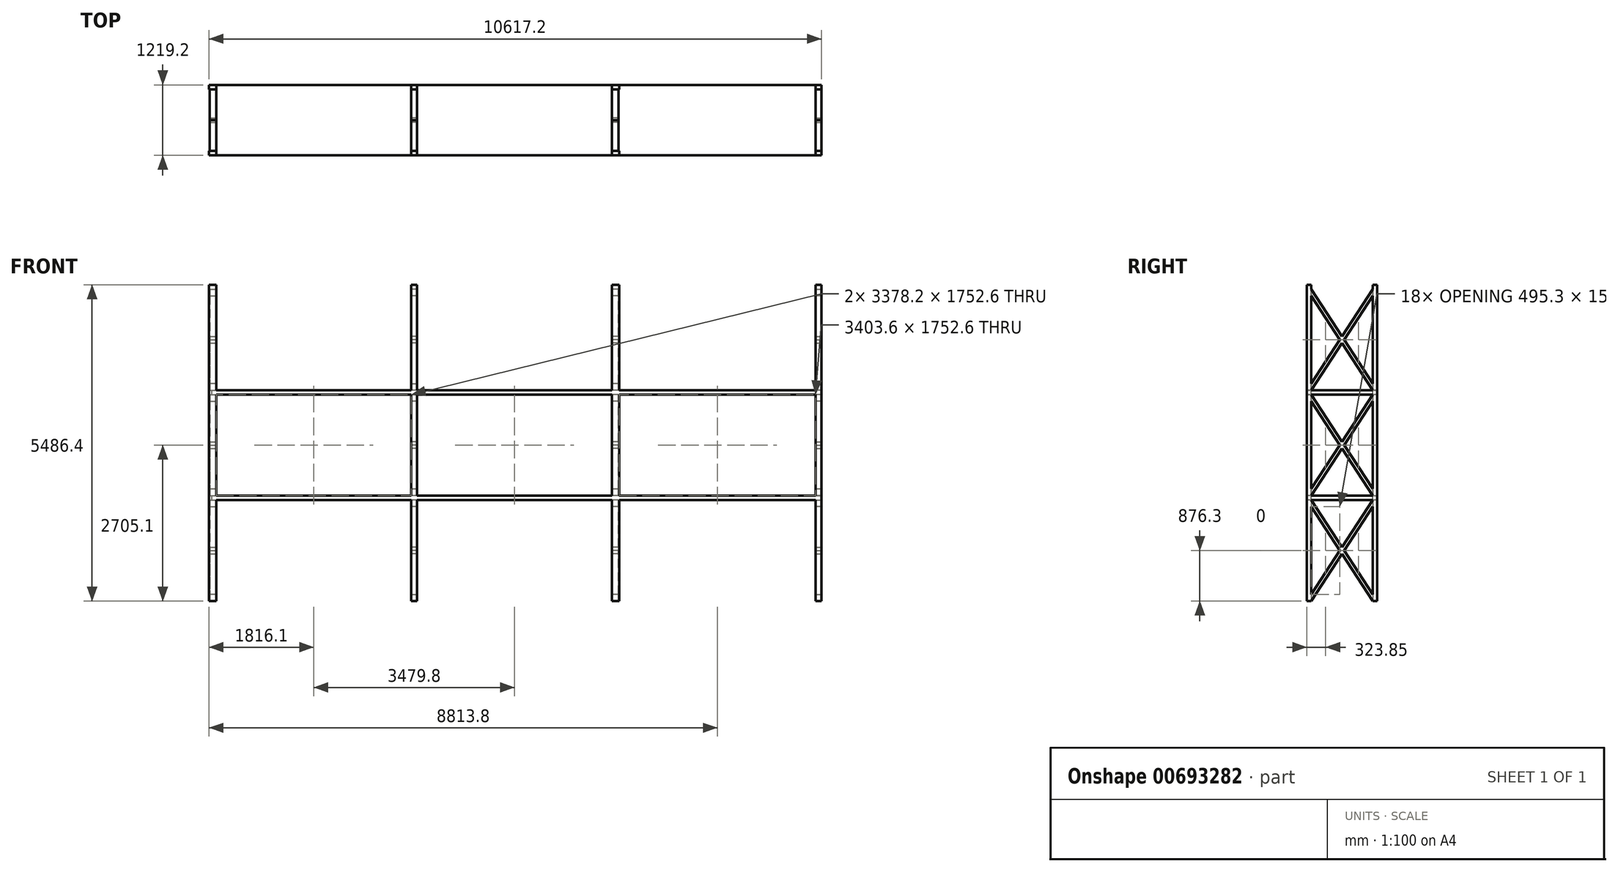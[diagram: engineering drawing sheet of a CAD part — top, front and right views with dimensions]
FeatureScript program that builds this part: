
annotation { "Feature Type Name" : "Feature", "Feature Type Description" : "" }
export const myFeature = defineFeature(function(context is Context, id is Id, definition is map)
    precondition{}
    {
        {
            var Q0;
            Q0=qCreatedBy(makeId("Front.planeOp"),FACE);
            var sketch = newSketch(context, id + "F0", { "sketchPlane" : qUnion([Q0])});
            skLineSegment(sketch, "E0.bottom", {"start": v(0, 0) * mm, "end": v(76.2, 0) * mm, "construction": true});
            skLineSegment(sketch, "E0.top", {"start": v(0, 5486.4) * mm, "end": v(76.2, 5486.4) * mm, "construction": true});
            skLineSegment(sketch, "E0.left", {"start": v(0, 0) * mm, "end": v(0, 5486.4) * mm, "construction": true});
            skLineSegment(sketch, "E0.right", {"start": v(76.2, 0) * mm, "end": v(76.2, 5486.4) * mm, "construction": true});
            skLineSegment(sketch, "E1.left", {"start": v(0, 5486.4) * mm, "end": v(0, 5410.2) * mm});
            skLineSegment(sketch, "E1.right", {"start": v(7010.4, 5486.4) * mm, "end": v(7010.4, 5410.2) * mm, "construction": true});
            skLineSegment(sketch, "E2.bottom", {"start": v(6934.2, 0) * mm, "end": v(7010.4, 0) * mm, "construction": true});
            skLineSegment(sketch, "E2.left", {"start": v(6934.2, 0) * mm, "end": v(6934.2, 5486.4) * mm, "construction": true});
            skLineSegment(sketch, "E2.right", {"start": v(7010.4, 0) * mm, "end": v(7010.4, 5334) * mm, "construction": true});
            skPoint(sketch, "E3", {"position": v(0, 1752.6) * mm});
            skPoint(sketch, "E4", {"position": v(0, 3581.4) * mm});
            skLineSegment(sketch, "E5.bottom", {"start": v(0, 1752.6) * mm, "end": v(7010.4, 1752.6) * mm});
            skLineSegment(sketch, "E5.top", {"start": v(0, 1828.8) * mm, "end": v(7010.4, 1828.8) * mm});
            skLineSegment(sketch, "E5.left", {"start": v(0, 1752.6) * mm, "end": v(0, 1828.8) * mm});
            skLineSegment(sketch, "E5.right", {"start": v(7010.4, 1752.6) * mm, "end": v(7010.4, 1828.8) * mm});
            skLineSegment(sketch, "E6.bottom", {"start": v(0, 3581.4) * mm, "end": v(7010.4, 3581.4) * mm});
            skLineSegment(sketch, "E6.top", {"start": v(0, 3657.6) * mm, "end": v(7010.4, 3657.6) * mm});
            skLineSegment(sketch, "E6.left", {"start": v(0, 3581.4) * mm, "end": v(0, 3657.6) * mm});
            skLineSegment(sketch, "E6.right", {"start": v(7010.4, 3581.4) * mm, "end": v(7010.4, 3657.6) * mm});
            skSolve(sketch);
        }
        {
            var Q0;
            Q0 = qSketchRegion(id + "F0", true);
            extrude(context, id + "F1", {"entities" : qUnion([Q0]), "oppositeDirection" : true, "depth" : 1219.2 * mm, "offsetDistance" : 25.4 * mm});
        }
        {
            var Q0;
            Q0=makeQuery(id+"F1.opExtrude","SWEPT_FACE",FACE,{"disambiguationData":[OSD([sQuery(id+"F0.wireOp",EDGE,"E6.left")])]});
            var sketch = newSketch(context, id + "F2", { "sketchPlane" : qUnion([Q0])});
            skLineSegment(sketch, "E7.bottom", {"start": v(0, 0) * mm, "end": v(-76.2, 0) * mm});
            skLineSegment(sketch, "E7.top", {"start": v(0, 5486.4) * mm, "end": v(-76.2, 5486.4) * mm});
            skLineSegment(sketch, "E7.left", {"start": v(0, 0) * mm, "end": v(0, 5486.4) * mm});
            skLineSegment(sketch, "E7.right", {"start": v(-76.2, 0) * mm, "end": v(-76.2, 5486.4) * mm});
            skLineSegment(sketch, "E8.bottom", {"start": v(-1219.2, 0) * mm, "end": v(-1143, 0) * mm});
            skLineSegment(sketch, "E8.top", {"start": v(-1219.2, 5486.4) * mm, "end": v(-1143, 5486.4) * mm});
            skLineSegment(sketch, "E8.left", {"start": v(-1219.2, 0) * mm, "end": v(-1219.2, 5486.4) * mm});
            skLineSegment(sketch, "E8.right", {"start": v(-1143, 0) * mm, "end": v(-1143, 5486.4) * mm});
            skSolve(sketch);
        }
        {
            var Q0;
            Q0 = qSketchRegion(id + "F2", true);
            extrude(context, id + "F3", {"entities" : qUnion([Q0]), "oppositeDirection" : true, "depth" : 76.2 * mm, "offsetDistance" : 25.4 * mm, "hasSecondDirection" : true, "secondDirectionOppositeDirection" : false, "secondDirectionDepth" : 50.8 * mm});
        }
        {
            var Q0;
            Q0=makeQuery(id+"F1.opExtrude","SWEPT_FACE",FACE,{"disambiguationData":[OSD([sQuery(id+"F0.wireOp",EDGE,"E6.right")])]});
            var sketch = newSketch(context, id + "F4", { "sketchPlane" : qUnion([Q0])});
            skLineSegment(sketch, "E9.bottom", {"start": v(0, 0) * mm, "end": v(76.2, 0) * mm});
            skLineSegment(sketch, "E9.top", {"start": v(0, 5486.4) * mm, "end": v(76.2, 5486.4) * mm});
            skLineSegment(sketch, "E9.left", {"start": v(0, 0) * mm, "end": v(0, 5486.4) * mm});
            skLineSegment(sketch, "E9.right", {"start": v(76.2, 0) * mm, "end": v(76.2, 5486.4) * mm});
            skLineSegment(sketch, "E10.bottom", {"start": v(1219.2, 0) * mm, "end": v(1143, 0) * mm});
            skLineSegment(sketch, "E10.top", {"start": v(1219.2, 5486.4) * mm, "end": v(1143, 5486.4) * mm});
            skLineSegment(sketch, "E10.left", {"start": v(1219.2, 0) * mm, "end": v(1219.2, 5486.4) * mm});
            skLineSegment(sketch, "E10.right", {"start": v(1143, 0) * mm, "end": v(1143, 5486.4) * mm});
            skSolve(sketch);
        }
        {
            var Q0;
            Q0 = qSketchRegion(id + "F4", true);
            extrude(context, id + "F5", {"entities" : qUnion([Q0]), "depth" : 50.8 * mm, "offsetDistance" : 25.4 * mm, "hasSecondDirection" : true, "secondDirectionOppositeDirection" : true, "secondDirectionDepth" : 76.2 * mm});
        }
        {
            var Q0;
            Q0=makeQuery(id+"F1.opExtrude","SWEPT_FACE",FACE,{"disambiguationData":[OSD([sQuery(id+"F0.wireOp",EDGE,"E5.left")])]});
            var sketch = newSketch(context, id + "F6", { "sketchPlane" : qUnion([Q0])});
            skPoint(sketch, "E11", {"position": v(-76.2, 0) * mm});
            skPoint(sketch, "E12", {"position": v(-1219.2, 1752.6) * mm});
            skPoint(sketch, "E13", {"position": v(-1219.2, 1828.8) * mm});
            skPoint(sketch, "E14", {"position": v(0, 1752.6) * mm});
            skPoint(sketch, "E15", {"position": v(-1219.2, 0) * mm});
            skPoint(sketch, "E16", {"position": v(-1143, 0) * mm});
            skLineSegment(sketch, "E17", {"start": v(-1219.2, 1752.6) * mm, "end": v(-76.2, 0) * mm});
            skLineSegment(sketch, "E18", {"start": v(0, 1752.6) * mm, "end": v(-1143, 0) * mm});
            skPoint(sketch, "E19", {"position": v(-76.2, 1828.8) * mm});
            skPoint(sketch, "E20", {"position": v(-1143, 1828.8) * mm});
            skPoint(sketch, "E21", {"position": v(-76.2, 1752.6) * mm});
            skPoint(sketch, "E22", {"position": v(-1143, 1752.6) * mm});
            skLineSegment(sketch, "E23", {"start": v(-1219.2, 1752.6) * mm, "end": v(-1143, 1752.6) * mm});
            skLineSegment(sketch, "E24", {"start": v(0, 1752.6) * mm, "end": v(-76.2, 1752.6) * mm});
            skLineSegment(sketch, "E25", {"start": v(-1143, 0) * mm, "end": v(-1219.2, 0) * mm});
            skLineSegment(sketch, "E26", {"start": v(-1219.2, 0) * mm, "end": v(-76.2, 1752.6) * mm});
            skLineSegment(sketch, "E27", {"start": v(-1143, 1752.6) * mm, "end": v(0, 0) * mm});
            skLineSegment(sketch, "E28", {"start": v(-76.2, 0) * mm, "end": v(0, 0) * mm});
            skSolve(sketch);
        }
        {
            var Q0;
            Q0 = qSketchRegion(id + "F6", true);
            extrude(context, id + "F7", {"entities" : qUnion([Q0]), "depth" : 38.1 * mm, "offsetDistance" : 25.4 * mm, "hasSecondDirection" : true, "secondDirectionOppositeDirection" : true, "secondDirectionDepth" : 76.2 * mm});
        }
        {
            var Q0;
            Q0=makeQuery(id+"F1.opExtrude","SWEPT_FACE",FACE,{"disambiguationData":[OSD([sQuery(id+"F0.wireOp",EDGE,"E5.left")])]});
            var sketch = newSketch(context, id + "F8", { "sketchPlane" : qUnion([Q0])});
            skPoint(sketch, "E29", {"position": v(-1219.2, 3581.4) * mm});
            skLineSegment(sketch, "E30", {"start": v(-1219.2, 3581.4) * mm, "end": v(-76.2, 1828.8) * mm});
            skLineSegment(sketch, "E31", {"start": v(0, 3581.4) * mm, "end": v(-1143, 1828.8) * mm});
            skPoint(sketch, "E32", {"position": v(-1143, 3581.4) * mm});
            skLineSegment(sketch, "E33", {"start": v(-1219.2, 1828.8) * mm, "end": v(-76.2, 3581.4) * mm});
            skLineSegment(sketch, "E34", {"start": v(-1143, 3581.4) * mm, "end": v(0, 1828.8) * mm});
            skLineSegment(sketch, "E35", {"start": v(-1219.2, 3581.4) * mm, "end": v(-1143, 3581.4) * mm});
            skLineSegment(sketch, "E36", {"start": v(-76.2, 3581.4) * mm, "end": v(0, 3581.4) * mm});
            skLineSegment(sketch, "E37", {"start": v(-76.2, 1828.8) * mm, "end": v(0, 1828.8) * mm});
            skLineSegment(sketch, "E38", {"start": v(-1143, 1828.8) * mm, "end": v(-1219.2, 1828.8) * mm});
            skSolve(sketch);
        }
        {
            var Q0;
            Q0 = qSketchRegion(id + "F8", true);
            extrude(context, id + "F9", {"entities" : qUnion([Q0]), "depth" : 38.1 * mm, "offsetDistance" : 25.4 * mm, "hasSecondDirection" : true, "secondDirectionOppositeDirection" : true, "secondDirectionDepth" : 76.2 * mm});
        }
        {
            var Q0;
            Q0=makeQuery(id+"F1.opExtrude","SWEPT_FACE",FACE,{"disambiguationData":[OSD([sQuery(id+"F0.wireOp",EDGE,"E6.left")])]});
            var sketch = newSketch(context, id + "F10", { "sketchPlane" : qUnion([Q0])});
            skPoint(sketch, "E39", {"position": v(-1219.2, 5410.2) * mm});
            skLineSegment(sketch, "E40", {"start": v(-1219.2, 5410.2) * mm, "end": v(-76.2, 3657.6) * mm});
            skLineSegment(sketch, "E41", {"start": v(0, 5410.2) * mm, "end": v(-1143, 3657.6) * mm});
            skPoint(sketch, "E42", {"position": v(-1143, 5410.2) * mm});
            skLineSegment(sketch, "E43", {"start": v(-1219.2, 3657.6) * mm, "end": v(-76.2, 5410.2) * mm});
            skLineSegment(sketch, "E44", {"start": v(-1143, 5410.2) * mm, "end": v(0, 3657.6) * mm});
            skLineSegment(sketch, "E45", {"start": v(-1219.2, 5410.2) * mm, "end": v(-1143, 5410.2) * mm});
            skLineSegment(sketch, "E46", {"start": v(-76.2, 5410.2) * mm, "end": v(0, 5410.2) * mm});
            skLineSegment(sketch, "E47", {"start": v(-76.2, 3657.6) * mm, "end": v(0, 3657.6) * mm});
            skLineSegment(sketch, "E48", {"start": v(-1143, 3657.6) * mm, "end": v(-1219.2, 3657.6) * mm});
            skSolve(sketch);
        }
        {
            var Q0;
            Q0 = qSketchRegion(id + "F10", true);
            extrude(context, id + "F11", {"entities" : qUnion([Q0]), "depth" : 38.1 * mm, "offsetDistance" : 25.4 * mm, "hasSecondDirection" : true, "secondDirectionOppositeDirection" : true, "secondDirectionDepth" : 76.2 * mm});
        }
        {
            var Q0;
            Q0=makeQuery(id+"F1.opExtrude","SWEPT_FACE",FACE,{"disambiguationData":[OSD([sQuery(id+"F0.wireOp",EDGE,"E5.right")])]});
            var sketch = newSketch(context, id + "F12", { "sketchPlane" : qUnion([Q0])});
            skPoint(sketch, "E49", {"position": v(0, 1752.6) * mm});
            skLineSegment(sketch, "E50", {"start": v(0, 1752.6) * mm, "end": v(1143, 0) * mm});
            skLineSegment(sketch, "E51", {"start": v(1219.2, 1752.6) * mm, "end": v(76.2, 0) * mm});
            skPoint(sketch, "E52", {"position": v(76.2, 1752.6) * mm});
            skLineSegment(sketch, "E53", {"start": v(0, 0) * mm, "end": v(1143, 1752.6) * mm});
            skLineSegment(sketch, "E54", {"start": v(76.2, 1752.6) * mm, "end": v(1219.2, 0) * mm});
            skLineSegment(sketch, "E55", {"start": v(0, 1752.6) * mm, "end": v(76.2, 1752.6) * mm});
            skLineSegment(sketch, "E56", {"start": v(1143, 1752.6) * mm, "end": v(1219.2, 1752.6) * mm});
            skLineSegment(sketch, "E57", {"start": v(1143, 0) * mm, "end": v(1219.2, 0) * mm});
            skLineSegment(sketch, "E58", {"start": v(76.2, 0) * mm, "end": v(0, 0) * mm});
            skSolve(sketch);
        }
        {
            var Q0;
            Q0 = qSketchRegion(id + "F12", true);
            extrude(context, id + "F13", {"entities" : qUnion([Q0]), "depth" : 38.1 * mm, "offsetDistance" : 25.4 * mm, "hasSecondDirection" : true, "secondDirectionOppositeDirection" : true, "secondDirectionDepth" : 76.2 * mm});
        }
        {
            var Q0;
            Q0=makeQuery(id+"F1.opExtrude","SWEPT_FACE",FACE,{"disambiguationData":[OSD([sQuery(id+"F0.wireOp",EDGE,"E5.right")])]});
            var sketch = newSketch(context, id + "F14", { "sketchPlane" : qUnion([Q0])});
            skPoint(sketch, "E59", {"position": v(0, 3581.4) * mm});
            skLineSegment(sketch, "E60", {"start": v(0, 3581.4) * mm, "end": v(1143, 1828.8) * mm});
            skLineSegment(sketch, "E61", {"start": v(1219.2, 3581.4) * mm, "end": v(76.2, 1828.8) * mm});
            skPoint(sketch, "E62", {"position": v(76.2, 3581.4) * mm});
            skLineSegment(sketch, "E63", {"start": v(0, 1828.8) * mm, "end": v(1143, 3581.4) * mm});
            skLineSegment(sketch, "E64", {"start": v(76.2, 3581.4) * mm, "end": v(1219.2, 1828.8) * mm});
            skLineSegment(sketch, "E65", {"start": v(0, 3581.4) * mm, "end": v(76.2, 3581.4) * mm});
            skLineSegment(sketch, "E66", {"start": v(1143, 3581.4) * mm, "end": v(1219.2, 3581.4) * mm});
            skLineSegment(sketch, "E67", {"start": v(1143, 1828.8) * mm, "end": v(1219.2, 1828.8) * mm});
            skLineSegment(sketch, "E68", {"start": v(76.2, 1828.8) * mm, "end": v(0, 1828.8) * mm});
            skSolve(sketch);
        }
        {
            var Q0;
            Q0 = qSketchRegion(id + "F14", true);
            extrude(context, id + "F15", {"entities" : qUnion([Q0]), "depth" : 38.1 * mm, "offsetDistance" : 25.4 * mm, "hasSecondDirection" : true, "secondDirectionOppositeDirection" : true, "secondDirectionDepth" : 76.2 * mm});
        }
        {
            var Q0;
            Q0=makeQuery(id+"F1.opExtrude","SWEPT_FACE",FACE,{"disambiguationData":[OSD([sQuery(id+"F0.wireOp",EDGE,"E6.right")])]});
            var sketch = newSketch(context, id + "F16", { "sketchPlane" : qUnion([Q0])});
            skPoint(sketch, "E69", {"position": v(0, 5410.2) * mm});
            skLineSegment(sketch, "E70", {"start": v(0, 5410.2) * mm, "end": v(1143, 3657.6) * mm});
            skLineSegment(sketch, "E71", {"start": v(1219.2, 5410.2) * mm, "end": v(76.2, 3657.6) * mm});
            skPoint(sketch, "E72", {"position": v(76.2, 5410.2) * mm});
            skLineSegment(sketch, "E73", {"start": v(0, 3657.6) * mm, "end": v(1143, 5410.2) * mm});
            skLineSegment(sketch, "E74", {"start": v(76.2, 5410.2) * mm, "end": v(1219.2, 3657.6) * mm});
            skLineSegment(sketch, "E75", {"start": v(0, 5410.2) * mm, "end": v(76.2, 5410.2) * mm});
            skLineSegment(sketch, "E76", {"start": v(1143, 5410.2) * mm, "end": v(1219.2, 5410.2) * mm});
            skLineSegment(sketch, "E77", {"start": v(1143, 3657.6) * mm, "end": v(1219.2, 3657.6) * mm});
            skLineSegment(sketch, "E78", {"start": v(76.2, 3657.6) * mm, "end": v(0, 3657.6) * mm});
            skSolve(sketch);
        }
        {
            var Q0;
            Q0 = qSketchRegion(id + "F16", true);
            extrude(context, id + "F17", {"entities" : qUnion([Q0]), "depth" : 38.1 * mm, "offsetDistance" : 25.4 * mm, "hasSecondDirection" : true, "secondDirectionOppositeDirection" : true, "secondDirectionDepth" : 76.2 * mm});
        }
        {
            var Q0;
            Q0=makeQuery(id+"F1.opExtrude","CAP_FACE",FACE,{"disambiguationData":[OSD([sQuery(id+"F0.wireOp",EDGE,"E6.bottom"),sQuery(id+"F0.wireOp",EDGE,"E6.top"),sQuery(id+"F0.wireOp",EDGE,"E6.left"),sQuery(id+"F0.wireOp",EDGE,"E6.right")])],"isStart":true});
            var sketch = newSketch(context, id + "F18", { "sketchPlane" : qUnion([Q0])});
            skPoint(sketch, "E79", {"position": v(3505.2, 3581.4) * mm});
            skPoint(sketch, "E80", {"position": v(3454.4, 0) * mm});
            skLineSegment(sketch, "E81.bottom", {"start": v(3454.4, 0) * mm, "end": v(3556, 0) * mm});
            skLineSegment(sketch, "E81.top", {"start": v(3454.4, 5486.4) * mm, "end": v(3556, 5486.4) * mm});
            skLineSegment(sketch, "E81.left", {"start": v(3454.4, 0) * mm, "end": v(3454.4, 5486.4) * mm});
            skLineSegment(sketch, "E81.right", {"start": v(3556, 0) * mm, "end": v(3556, 5486.4) * mm});
            skSolve(sketch);
        }
        {
            var Q0;
            Q0 = qSketchRegion(id + "F18", true);
            extrude(context, id + "F19", {"entities" : qUnion([Q0]), "oppositeDirection" : true, "depth" : 76.2 * mm, "offsetDistance" : 25.4 * mm});
        }
        {
            var Q0;
            Q0=makeQuery(id+"F1.opExtrude","CAP_FACE",FACE,{"disambiguationData":[OSD([sQuery(id+"F0.wireOp",EDGE,"E6.bottom"),sQuery(id+"F0.wireOp",EDGE,"E6.top"),sQuery(id+"F0.wireOp",EDGE,"E6.left"),sQuery(id+"F0.wireOp",EDGE,"E6.right")])],"isStart":false});
            var sketch = newSketch(context, id + "F20", { "sketchPlane" : qUnion([Q0])});
            skPoint(sketch, "E82", {"position": v(-3505.2, 3581.4) * mm});
            skPoint(sketch, "E83", {"position": v(-3505.2, 0) * mm});
            skPoint(sketch, "E84", {"position": v(-3556, 0) * mm});
            skLineSegment(sketch, "E85.bottom", {"start": v(-3556, 0) * mm, "end": v(-3454.4, 0) * mm});
            skLineSegment(sketch, "E85.top", {"start": v(-3556, 5486.4) * mm, "end": v(-3454.4, 5486.4) * mm});
            skLineSegment(sketch, "E85.left", {"start": v(-3556, 0) * mm, "end": v(-3556, 5486.4) * mm});
            skLineSegment(sketch, "E85.right", {"start": v(-3454.4, 0) * mm, "end": v(-3454.4, 5486.4) * mm});
            skSolve(sketch);
        }
        {
            var Q0;
            Q0 = qSketchRegion(id + "F20", true);
            extrude(context, id + "F21", {"entities" : qUnion([Q0]), "oppositeDirection" : true, "depth" : 76.2 * mm, "offsetDistance" : 25.4 * mm});
        }
        {
            var Q0;
            Q0=makeQuery(id+"F21.opExtrude","SWEPT_FACE",FACE,{"disambiguationData":[OSD([sQuery(id+"F20.wireOp",EDGE,"E85.right")])]});
            var sketch = newSketch(context, id + "F22", { "sketchPlane" : qUnion([Q0])});
            skPoint(sketch, "E86", {"position": v(-1219.2, 1752.6) * mm});
            skLineSegment(sketch, "E87", {"start": v(-1219.2, 1752.6) * mm, "end": v(-647.7, 876.3) * mm});
            skLineSegment(sketch, "E88", {"start": v(0, 1752.6) * mm, "end": v(-571.5, 876.3) * mm});
            skPoint(sketch, "E89", {"position": v(-1143, 1752.6) * mm});
            skLineSegment(sketch, "E90", {"start": v(-1219.2, 0) * mm, "end": v(-647.7, 876.3) * mm});
            skLineSegment(sketch, "E91", {"start": v(-1143, 1752.6) * mm, "end": v(-609.6, 934.72) * mm});
            skLineSegment(sketch, "E92", {"start": v(-1219.2, 1752.6) * mm, "end": v(-1143, 1752.6) * mm});
            skLineSegment(sketch, "E93", {"start": v(-76.2, 1752.6) * mm, "end": v(0, 1752.6) * mm});
            skLineSegment(sketch, "E94", {"start": v(-76.2, 0) * mm, "end": v(0, 0) * mm});
            skLineSegment(sketch, "E95", {"start": v(-1143, 0) * mm, "end": v(-1219.2, 0) * mm});
            skPoint(sketch, "E96", {"position": v(-609.6, 934.72) * mm});
            skPoint(sketch, "E97", {"position": v(-571.5, 876.3) * mm});
            skPoint(sketch, "E98", {"position": v(-609.6, 817.88) * mm});
            skPoint(sketch, "E99", {"position": v(-647.7, 876.3) * mm});
            skLineSegment(sketch, "E100.trimOffspring", {"start": v(-571.5, 876.3) * mm, "end": v(0, 0) * mm});
            skLineSegment(sketch, "E101.trimOffspring", {"start": v(-609.6, 817.88) * mm, "end": v(-1143, 0) * mm});
            skLineSegment(sketch, "E102.trimOffspring", {"start": v(-609.6, 817.88) * mm, "end": v(-76.2, 0) * mm});
            skLineSegment(sketch, "E103.trimOffspring", {"start": v(-609.6, 934.72) * mm, "end": v(-76.2, 1752.6) * mm});
            skSolve(sketch);
        }
        {
            var Q0;
            Q0 = qSketchRegion(id + "F22", true);
            extrude(context, id + "F23", {"entities" : qUnion([Q0]), "oppositeDirection" : true, "depth" : 101.6 * mm, "offsetDistance" : 25.4 * mm});
        }
        {
            var Q0;
            Q0=makeQuery(id+"F21.opExtrude","SWEPT_FACE",FACE,{"disambiguationData":[OSD([sQuery(id+"F20.wireOp",EDGE,"E85.right")])]});
            var sketch = newSketch(context, id + "F24", { "sketchPlane" : qUnion([Q0])});
            skPoint(sketch, "E104", {"position": v(-1219.2, 3581.66) * mm});
            skLineSegment(sketch, "E105", {"start": v(-1219.2, 3581.66) * mm, "end": v(-647.7, 2705.36) * mm});
            skLineSegment(sketch, "E106", {"start": v(0, 3581.66) * mm, "end": v(-571.5, 2705.36) * mm});
            skPoint(sketch, "E107", {"position": v(-1143, 3581.66) * mm});
            skLineSegment(sketch, "E108", {"start": v(-1219.2, 1829.06) * mm, "end": v(-647.7, 2705.36) * mm});
            skLineSegment(sketch, "E109", {"start": v(-1143, 3581.66) * mm, "end": v(-609.6, 2763.78) * mm});
            skLineSegment(sketch, "E110", {"start": v(-1219.2, 3581.66) * mm, "end": v(-1143, 3581.66) * mm});
            skLineSegment(sketch, "E111", {"start": v(-76.2, 3581.66) * mm, "end": v(0, 3581.66) * mm});
            skLineSegment(sketch, "E112", {"start": v(-76.2, 1829.06) * mm, "end": v(0, 1829.06) * mm});
            skLineSegment(sketch, "E113", {"start": v(-1143, 1829.06) * mm, "end": v(-1219.2, 1829.06) * mm});
            skPoint(sketch, "E114", {"position": v(-609.6, 2763.78) * mm});
            skPoint(sketch, "E115", {"position": v(-571.5, 2705.36) * mm});
            skPoint(sketch, "E116", {"position": v(-609.6, 2646.94) * mm});
            skPoint(sketch, "E117", {"position": v(-647.7, 2705.36) * mm});
            skLineSegment(sketch, "E118.trimOffspring", {"start": v(-571.5, 2705.36) * mm, "end": v(0, 1829.06) * mm});
            skLineSegment(sketch, "E119.trimOffspring", {"start": v(-609.6, 2646.94) * mm, "end": v(-1143, 1829.06) * mm});
            skLineSegment(sketch, "E120.trimOffspring", {"start": v(-609.6, 2646.94) * mm, "end": v(-76.2, 1829.06) * mm});
            skLineSegment(sketch, "E121.trimOffspring", {"start": v(-609.6, 2763.78) * mm, "end": v(-76.2, 3581.66) * mm});
            skSolve(sketch);
        }
        {
            var Q0;
            Q0 = qSketchRegion(id + "F24", true);
            extrude(context, id + "F25", {"entities" : qUnion([Q0]), "oppositeDirection" : true, "depth" : 101.6 * mm, "offsetDistance" : 25.4 * mm});
        }
        {
            var Q0;
            Q0=makeQuery(id+"F21.opExtrude","SWEPT_FACE",FACE,{"disambiguationData":[OSD([sQuery(id+"F20.wireOp",EDGE,"E85.right")])]});
            var sketch = newSketch(context, id + "F26", { "sketchPlane" : qUnion([Q0])});
            skPoint(sketch, "E122", {"position": v(-1219.2, 5409.1) * mm});
            skLineSegment(sketch, "E123", {"start": v(-1219.2, 5409.1) * mm, "end": v(-647.7, 4532.8) * mm});
            skLineSegment(sketch, "E124", {"start": v(0, 5409.1) * mm, "end": v(-571.5, 4532.8) * mm});
            skPoint(sketch, "E125", {"position": v(-1143, 5409.1) * mm});
            skLineSegment(sketch, "E126", {"start": v(-1219.2, 3656.5) * mm, "end": v(-647.7, 4532.8) * mm});
            skLineSegment(sketch, "E127", {"start": v(-1143, 5409.1) * mm, "end": v(-609.6, 4591.22) * mm});
            skLineSegment(sketch, "E128", {"start": v(-1219.2, 5409.1) * mm, "end": v(-1143, 5409.1) * mm});
            skLineSegment(sketch, "E129", {"start": v(-76.2, 5409.1) * mm, "end": v(0, 5409.1) * mm});
            skLineSegment(sketch, "E130", {"start": v(-76.2, 3656.5) * mm, "end": v(0, 3656.5) * mm});
            skLineSegment(sketch, "E131", {"start": v(-1143, 3656.5) * mm, "end": v(-1219.2, 3656.5) * mm});
            skPoint(sketch, "E132", {"position": v(-609.6, 4591.22) * mm});
            skPoint(sketch, "E133", {"position": v(-571.5, 4532.8) * mm});
            skPoint(sketch, "E134", {"position": v(-609.6, 4474.38) * mm});
            skPoint(sketch, "E135", {"position": v(-647.7, 4532.8) * mm});
            skLineSegment(sketch, "E136.trimOffspring", {"start": v(-571.5, 4532.8) * mm, "end": v(0, 3656.5) * mm});
            skLineSegment(sketch, "E137.trimOffspring", {"start": v(-609.6, 4474.38) * mm, "end": v(-1143, 3656.5) * mm});
            skLineSegment(sketch, "E138.trimOffspring", {"start": v(-609.6, 4474.38) * mm, "end": v(-76.2, 3656.5) * mm});
            skLineSegment(sketch, "E139.trimOffspring", {"start": v(-609.6, 4591.22) * mm, "end": v(-76.2, 5409.1) * mm});
            skSolve(sketch);
        }
        {
            var Q0;
            Q0 = qSketchRegion(id + "F26", true);
            extrude(context, id + "F27", {"entities" : qUnion([Q0]), "oppositeDirection" : true, "depth" : 101.6 * mm, "offsetDistance" : 25.4 * mm});
        }
        {
            var Q0;
            Q0=makeQuery(id+"F21.opExtrude","SWEPT_BODY",BODY,{"disambiguationData":[OSD([sQuery(id+"F20.wireOp",EDGE,"E85.bottom"),sQuery(id+"F20.wireOp",EDGE,"E85.top"),sQuery(id+"F20.wireOp",EDGE,"E85.left"),sQuery(id+"F20.wireOp",EDGE,"E85.right")])]});
            var Q1;
            Q1=makeQuery(id+"F27.opExtrude","SWEPT_BODY",BODY,{"disambiguationData":[OSD([sQuery(id+"F26.wireOp",EDGE,"E123"),sQuery(id+"F26.wireOp",EDGE,"E124"),sQuery(id+"F26.wireOp",EDGE,"E126"),sQuery(id+"F26.wireOp",EDGE,"E127"),sQuery(id+"F26.wireOp",EDGE,"E128"),sQuery(id+"F26.wireOp",EDGE,"E129"),sQuery(id+"F26.wireOp",EDGE,"E130"),sQuery(id+"F26.wireOp",EDGE,"E131"),sQuery(id+"F26.wireOp",EDGE,"E136.trimOffspring"),sQuery(id+"F26.wireOp",EDGE,"E137.trimOffspring"),sQuery(id+"F26.wireOp",EDGE,"E138.trimOffspring"),sQuery(id+"F26.wireOp",EDGE,"E139.trimOffspring")])]});
            var Q2;
            Q2=makeQuery(id+"F19.opExtrude","SWEPT_BODY",BODY,{"disambiguationData":[OSD([sQuery(id+"F18.wireOp",EDGE,"E81.bottom"),sQuery(id+"F18.wireOp",EDGE,"E81.top"),sQuery(id+"F18.wireOp",EDGE,"E81.left"),sQuery(id+"F18.wireOp",EDGE,"E81.right")])]});
            var Q3;
            Q3=makeQuery(id+"F25.opExtrude","SWEPT_BODY",BODY,{"disambiguationData":[OSD([sQuery(id+"F24.wireOp",EDGE,"E105"),sQuery(id+"F24.wireOp",EDGE,"E106"),sQuery(id+"F24.wireOp",EDGE,"E108"),sQuery(id+"F24.wireOp",EDGE,"E109"),sQuery(id+"F24.wireOp",EDGE,"E110"),sQuery(id+"F24.wireOp",EDGE,"E111"),sQuery(id+"F24.wireOp",EDGE,"E112"),sQuery(id+"F24.wireOp",EDGE,"E113"),sQuery(id+"F24.wireOp",EDGE,"E118.trimOffspring"),sQuery(id+"F24.wireOp",EDGE,"E119.trimOffspring"),sQuery(id+"F24.wireOp",EDGE,"E120.trimOffspring"),sQuery(id+"F24.wireOp",EDGE,"E121.trimOffspring")])]});
            var Q4;
            Q4=makeQuery(id+"F23.opExtrude","SWEPT_BODY",BODY,{"disambiguationData":[OSD([sQuery(id+"F22.wireOp",EDGE,"E87"),sQuery(id+"F22.wireOp",EDGE,"E88"),sQuery(id+"F22.wireOp",EDGE,"E90"),sQuery(id+"F22.wireOp",EDGE,"E91"),sQuery(id+"F22.wireOp",EDGE,"E92"),sQuery(id+"F22.wireOp",EDGE,"E93"),sQuery(id+"F22.wireOp",EDGE,"E94"),sQuery(id+"F22.wireOp",EDGE,"E95"),sQuery(id+"F22.wireOp",EDGE,"E100.trimOffspring"),sQuery(id+"F22.wireOp",EDGE,"E101.trimOffspring"),sQuery(id+"F22.wireOp",EDGE,"E102.trimOffspring"),sQuery(id+"F22.wireOp",EDGE,"E103.trimOffspring")])]});
            var Q5;
            Q5=makeQuery(id+"F1.opExtrude","SWEPT_FACE",FACE,{"disambiguationData":[OSD([sQuery(id+"F0.wireOp",EDGE,"E6.right")])]});
            mirror(context, id + "F28", {"entities" : qUnion([Q0, Q1, Q2, Q3, Q4]), "mirrorPlane" : qUnion([Q5])});
        }
        {
            var Q0;
            Q0=makeQuery(id+"F1.opExtrude","SWEPT_FACE",FACE,{"disambiguationData":[OSD([sQuery(id+"F0.wireOp",EDGE,"E6.right")])]});
            cPlane(context, id + "F29", {"entities" : qUnion([Q0]), "cplaneType" : CPlaneType.OFFSET, "offset" : 0 * mm, "width" : 152.4 * mm, "height" : 152.4 * mm});
        }
        {
            var Q0;
            Q0=makeQuery(id+"F1.opExtrude","SWEPT_BODY",BODY,{"disambiguationData":[OSD([sQuery(id+"F0.wireOp",EDGE,"E6.bottom"),sQuery(id+"F0.wireOp",EDGE,"E6.top"),sQuery(id+"F0.wireOp",EDGE,"E6.left"),sQuery(id+"F0.wireOp",EDGE,"E6.right")])]});
            var Q1;
            Q1=makeQuery(id+"F1.opExtrude","SWEPT_BODY",BODY,{"disambiguationData":[OSD([sQuery(id+"F0.wireOp",EDGE,"E5.bottom"),sQuery(id+"F0.wireOp",EDGE,"E5.top"),sQuery(id+"F0.wireOp",EDGE,"E5.left"),sQuery(id+"F0.wireOp",EDGE,"E5.right")])]});
            var Q2;
            Q2=qCreatedBy(id+"F29.planeOp",FACE);
            mirror(context, id + "F30", {"operationType" : NewBodyOperationType.ADD, "entities" : qUnion([Q0, Q1]), "mirrorPlane" : qUnion([Q2])});
        }
        {
            var Q0;
            {var subQ0=makeQuery(id+"F1.opExtrude","SWEPT_FACE",FACE,{"disambiguationData":[OSD([sQuery(id+"F0.wireOp",EDGE,"E6.top")])]});Q0=makeQuery(id+"F30.boolean.opBoolean","MERGE",FACE,{"derivedFrom":[subQ0,makeQuery(id+"F30.opPattern","COPY",FACE,{"derivedFrom":subQ0,"instanceName":"1"})]});}
            var sketch = newSketch(context, id + "F31", { "sketchPlane" : qUnion([Q0])});
            skLineSegment(sketch, "E140.bottom", {"start": v(14020.8, 0) * mm, "end": v(10566.4, 0) * mm});
            skLineSegment(sketch, "E140.top", {"start": v(14020.8, 1219.2) * mm, "end": v(10566.4, 1219.2) * mm});
            skLineSegment(sketch, "E140.left", {"start": v(14020.8, 0) * mm, "end": v(14020.8, 1219.2) * mm});
            skLineSegment(sketch, "E140.right", {"start": v(10566.4, 0) * mm, "end": v(10566.4, 1219.2) * mm});
            skSolve(sketch);
        }
        {
            var Q0;
            Q0 = qSketchRegion(id + "F31", true);
            extrude(context, id + "F32", {"entities" : qUnion([Q0]), "operationType" : NewBodyOperationType.REMOVE, "endBound" : BoundingType.THROUGH_ALL, "oppositeDirection" : true, "depth" : 25.4 * mm, "offsetDistance" : 25.4 * mm});
        }
    });
